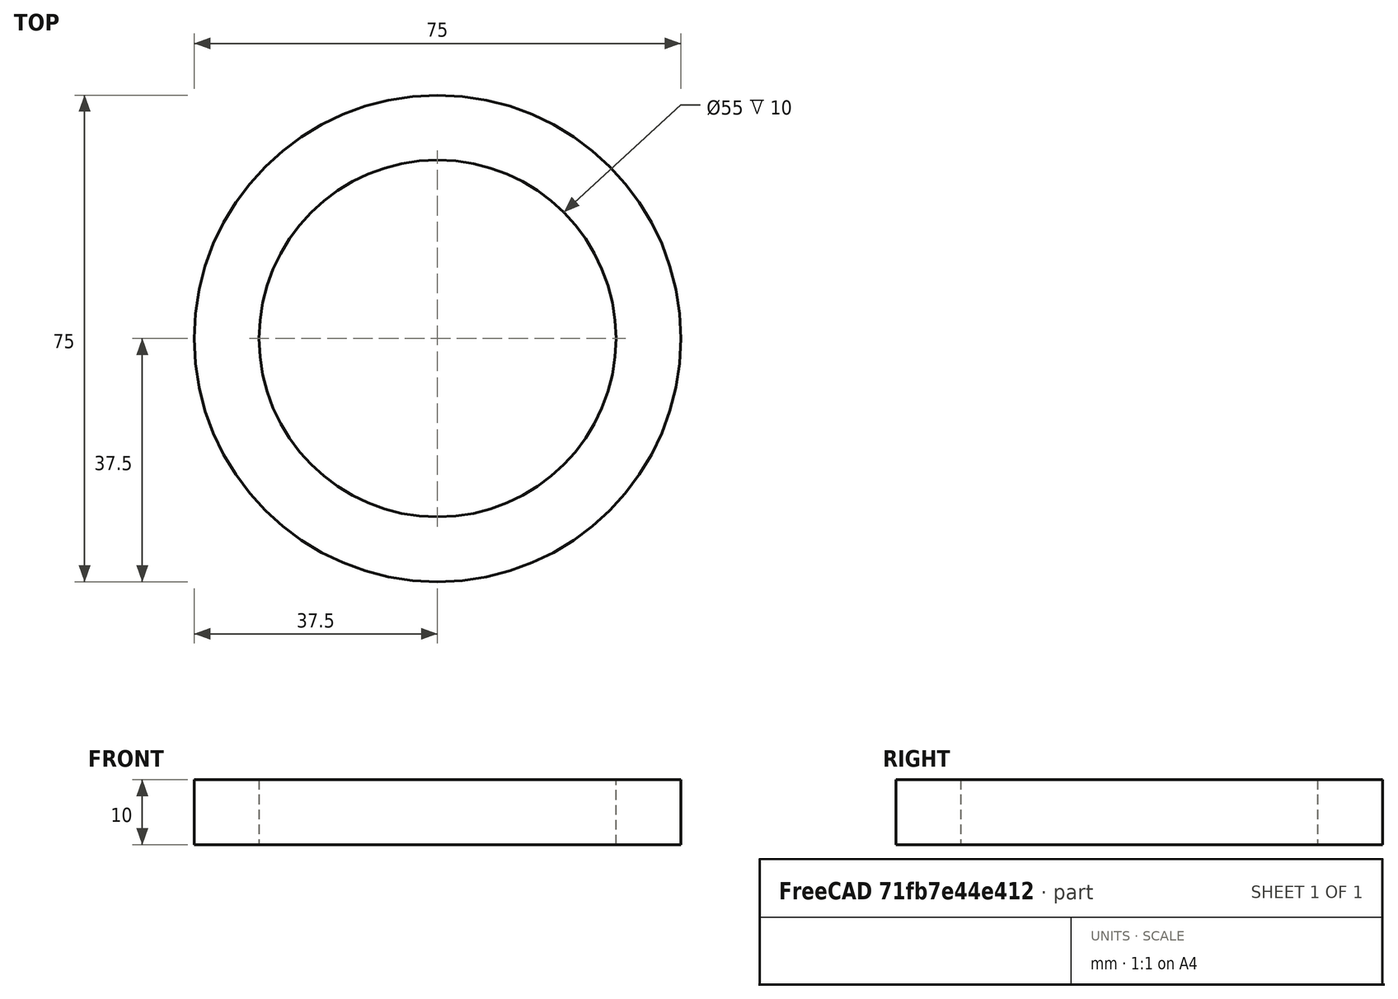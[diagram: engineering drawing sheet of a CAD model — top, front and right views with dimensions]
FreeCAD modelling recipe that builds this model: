
FCSTD DOCUMENT  (FreeCAD 0.19R24276 (Git))
Label: ring_75x55x10
License: All rights reserved
LicenseURL: http://en.wikipedia.org/wiki/All_rights_reserved
objects: Sketcher::SketchObject×1, PartDesign::Pad×1, PartDesign::Body×1
note: 4 computed .brp shape members not serialized (recipe doc carries the construction recipe); baked Part::Feature solids carry a one-line shape summary decoded from their .brp

FEATURE [Sketcher::SketchObject] Sketch
  FullyConstrained = true
  MapMode = 5
  Support = -> [XY_Plane]
  sketch-geometry (2):
    g0: Circle CenterX=0 CenterY=0 CenterZ=0 NormalX=0 NormalY=0 NormalZ=1 AngleXU=0 Radius=37.5
    g1: Circle CenterX=0 CenterY=0 CenterZ=0 NormalX=0 NormalY=0 NormalZ=1 AngleXU=0 Radius=27.5
  constraints (4):
    c: Coincident(g-1,g0)
    c: Coincident(g0,g1)
    c: Diameter(g1) = 55
    c: Diameter(g0) = 75
FEATURE [PartDesign::Pad] Pad
  Direction = (1,1,1)
  Length = 10
  Length2 = 100
  Profile = -> Sketch
  Type = 0
FEATURE [PartDesign::Body] Body
  Group = -> [Sketch,Pad]
  Origin = -> Origin
  Tip = -> Pad
